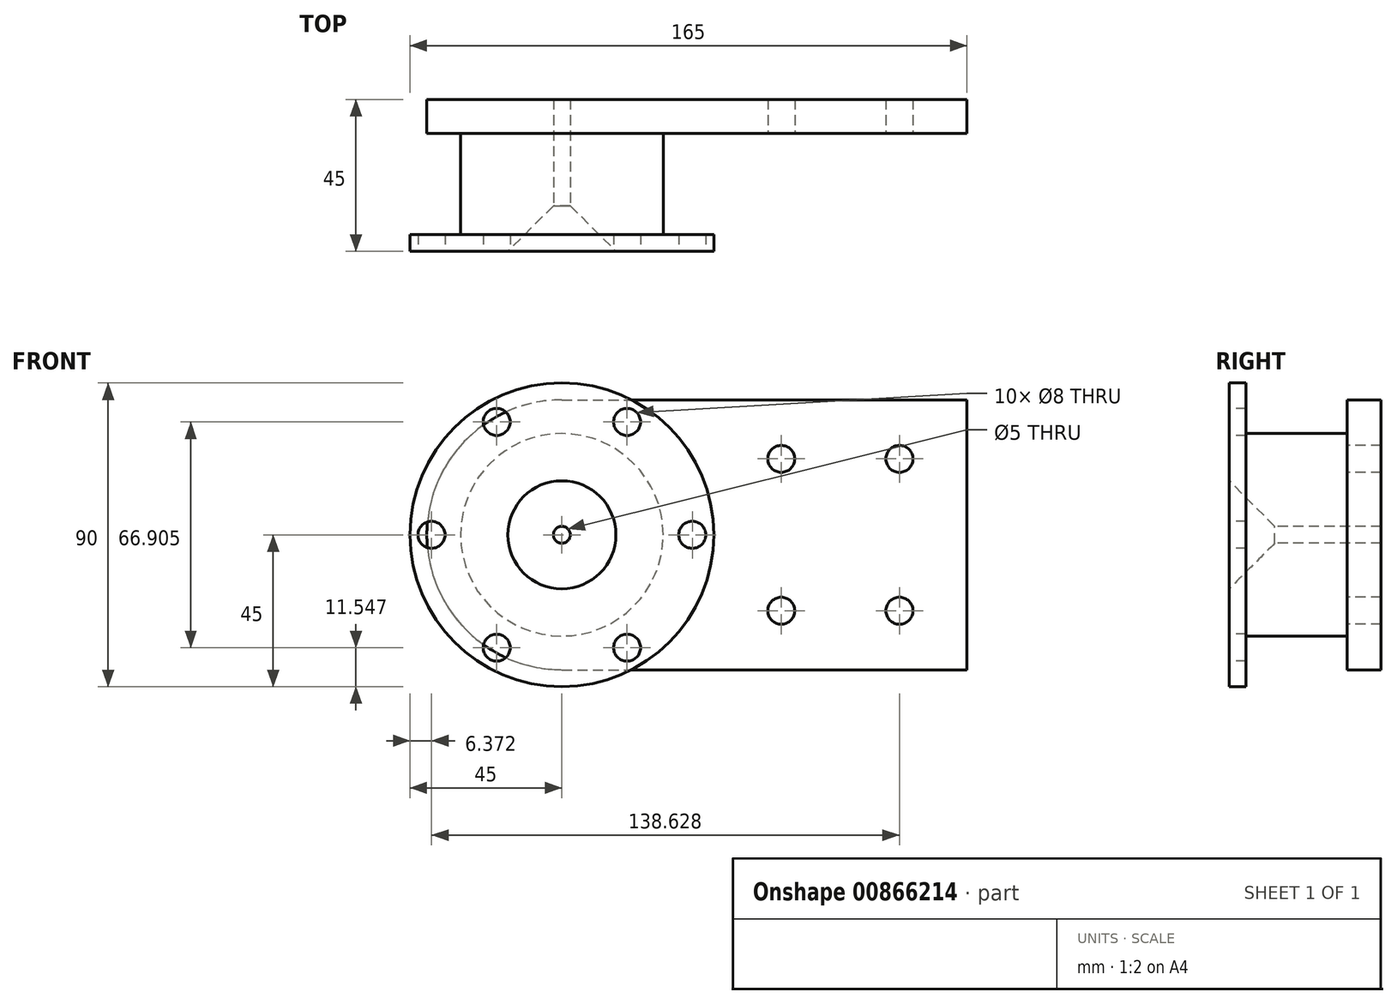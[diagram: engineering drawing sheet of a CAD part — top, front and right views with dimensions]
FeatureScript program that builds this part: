
annotation { "Feature Type Name" : "Feature", "Feature Type Description" : "" }
export const myFeature = defineFeature(function(context is Context, id is Id, definition is map)
    precondition{}
    {
        {
            var Q0;
            Q0=qCreatedBy(makeId("Front.planeOp"),FACE);
            var sketch = newSketch(context, id + "F0", { "sketchPlane" : qUnion([Q0])});
            skArc(sketch, "E0", {"start": v(0, 40) * mm, "mid": v(-40, 0) * mm, "end": v(0, -40) * mm});
            skLineSegment(sketch, "E1", {"start": v(0, 40) * mm, "end": v(120, 40) * mm});
            skLineSegment(sketch, "E2", {"start": v(120, 40) * mm, "end": v(120, -40) * mm});
            skLineSegment(sketch, "E3", {"start": v(0, -40) * mm, "end": v(120, -40) * mm});
            skSolve(sketch);
        }
        {
            var Q0;
            Q0=makeQuery(id+"F0.imprint","IMPRINT",FACE,{"disambiguationData":[TD([[makeQuery(id+"F0.imprint","IMPRINT",EDGE,{"derivedFrom":sQuery(id+"F0.wireOp",EDGE,"E0")}),1.0]])]});
            extrude(context, id + "F1", {"entities" : qUnion([Q0]), "depth" : 10 * mm, "offsetDistance" : 25 * mm});
        }
        {
            var Q0;
            Q0=makeQuery(id+"F1.opExtrude","CAP_FACE",FACE,{"disambiguationData":[OSD([sQuery(id+"F0.wireOp",EDGE,"E0"),sQuery(id+"F0.wireOp",EDGE,"E1"),sQuery(id+"F0.wireOp",EDGE,"E2"),sQuery(id+"F0.wireOp",EDGE,"E3")])],"isStart":false});
            var sketch = newSketch(context, id + "F2", { "sketchPlane" : qUnion([Q0])});
            skCircle(sketch, "E4", {"center": v(0, 0) * mm, "radius": 30 * mm});
            skSolve(sketch);
        }
        {
            var Q0;
            Q0 = qSketchRegion(id + "F2", true);
            extrude(context, id + "F3", {"entities" : qUnion([Q0]), "operationType" : NewBodyOperationType.ADD, "depth" : 30 * mm, "offsetDistance" : 25 * mm});
        }
        {
            var Q0;
            Q0=makeQuery(id+"F3.opExtrude","CAP_FACE",FACE,{"disambiguationData":[OSD([sQuery(id+"F2.wireOp",EDGE,"E4")])],"isStart":false});
            var sketch = newSketch(context, id + "F4", { "sketchPlane" : qUnion([Q0])});
            skCircle(sketch, "E5.0", {"center": v(0, 0) * mm, "radius": 45 * mm});
            skSolve(sketch);
        }
        {
            var Q0;
            Q0=makeQuery(id+"F4.imprint","IMPRINT",FACE,{"disambiguationData":[TD([[makeQuery(id+"F4.imprint","IMPRINT",EDGE,{"derivedFrom":makeQuery(id+"F3.opExtrude","CAP_EDGE",EDGE,{"disambiguationData":[OSD([sQuery(id+"F2.wireOp",EDGE,"E4")])],"isStart":false})}),1.0]])]});
            var Q1;
            Q1=makeQuery(id+"F4.imprint","IMPRINT",FACE,{"disambiguationData":[TD([[makeQuery(id+"F4.imprint","IMPRINT",EDGE,{"derivedFrom":sQuery(id+"F4.wireOp",EDGE,"E5.0")}),1.0]])]});
            extrude(context, id + "F5", {"entities" : qUnion([Q0, Q1]), "operationType" : NewBodyOperationType.ADD, "depth" : 5 * mm, "offsetDistance" : 25 * mm});
        }
        {
            var Q0;
            Q0=makeQuery(id+"F5.opExtrude","CAP_FACE",FACE,{"disambiguationData":[OSD([sQuery(id+"F4.wireOp",EDGE,"E5.0")])],"isStart":false});
            var sketch = newSketch(context, id + "F6", { "sketchPlane" : qUnion([Q0])});
            skLineSegment(sketch, "E6", {"start": v(0, 0) * mm, "end": v(45, 0) * mm, "construction": true});
            skCircle(sketch, "E7", {"center": v(38.63, 0) * mm, "radius": 4 * mm});
            skCircle(sketch, "E8.1.0", {"center": v(19.31, 33.45) * mm, "radius": 4 * mm});
            skCircle(sketch, "E8.2.0", {"center": v(-19.31, 33.45) * mm, "radius": 4 * mm});
            skCircle(sketch, "E8.3.0", {"center": v(-38.63, 0) * mm, "radius": 4 * mm});
            skCircle(sketch, "E8.4.0", {"center": v(-19.31, -33.45) * mm, "radius": 4 * mm});
            skCircle(sketch, "E8.5.0", {"center": v(19.31, -33.45) * mm, "radius": 4 * mm});
            skPoint(sketch, "E8.center", {"position": v(0, 0) * mm});
            skSolve(sketch);
        }
        {
            var Q0;
            Q0=makeQuery(id+"F6.imprint","IMPRINT",FACE,{"disambiguationData":[TD([[makeQuery(id+"F6.imprint","IMPRINT",EDGE,{"derivedFrom":sQuery(id+"F6.wireOp",EDGE,"E8.2.0")}),1.0]])]});
            var Q1;
            Q1=makeQuery(id+"F6.imprint","IMPRINT",FACE,{"disambiguationData":[TD([[makeQuery(id+"F6.imprint","IMPRINT",EDGE,{"derivedFrom":sQuery(id+"F6.wireOp",EDGE,"E8.1.0")}),1.0]])]});
            var Q2;
            Q2=makeQuery(id+"F6.imprint","IMPRINT",FACE,{"disambiguationData":[TD([[makeQuery(id+"F6.imprint","IMPRINT",EDGE,{"derivedFrom":sQuery(id+"F6.wireOp",EDGE,"E7")}),1.0]])]});
            var Q3;
            Q3=makeQuery(id+"F6.imprint","IMPRINT",FACE,{"disambiguationData":[TD([[makeQuery(id+"F6.imprint","IMPRINT",EDGE,{"derivedFrom":sQuery(id+"F6.wireOp",EDGE,"E8.5.0")}),1.0]])]});
            var Q4;
            Q4=makeQuery(id+"F6.imprint","IMPRINT",FACE,{"disambiguationData":[TD([[makeQuery(id+"F6.imprint","IMPRINT",EDGE,{"derivedFrom":sQuery(id+"F6.wireOp",EDGE,"E8.4.0")}),1.0]])]});
            var Q5;
            Q5=makeQuery(id+"F6.imprint","IMPRINT",FACE,{"disambiguationData":[TD([[makeQuery(id+"F6.imprint","IMPRINT",EDGE,{"derivedFrom":sQuery(id+"F6.wireOp",EDGE,"E8.3.0")}),1.0]])]});
            var Q6;
            Q6=makeQuery(id+"F5.opExtrude","CAP_FACE",FACE,{"disambiguationData":[OSD([sQuery(id+"F4.wireOp",EDGE,"E5.0")])],"isStart":true});
            extrude(context, id + "F7", {"entities" : qUnion([Q0, Q1, Q2, Q3, Q4, Q5]), "operationType" : NewBodyOperationType.REMOVE, "endBound" : BoundingType.UP_TO_SURFACE, "oppositeDirection" : true, "depth" : 25 * mm, "endBoundEntityFace" : qUnion([Q6]), "offsetDistance" : 25 * mm});
        }
        {
            var Q0;
            Q0=makeQuery(id+"F1.opExtrude","CAP_FACE",FACE,{"disambiguationData":[OSD([sQuery(id+"F0.wireOp",EDGE,"E0"),sQuery(id+"F0.wireOp",EDGE,"E1"),sQuery(id+"F0.wireOp",EDGE,"E2"),sQuery(id+"F0.wireOp",EDGE,"E3")])],"isStart":false});
            var sketch = newSketch(context, id + "F8", { "sketchPlane" : qUnion([Q0])});
            skLineSegment(sketch, "E9", {"start": v(120, 0) * mm, "end": v(45.7, 0) * mm, "construction": true});
            skLineSegment(sketch, "E10", {"start": v(120, 22.5) * mm, "end": v(49.41, 22.5) * mm, "construction": true});
            skCircle(sketch, "E11", {"center": v(65, 22.5) * mm, "radius": 4 * mm});
            skCircle(sketch, "E12", {"center": v(100, 22.5) * mm, "radius": 4 * mm});
            skCircle(sketch, "E13.MirrorC", {"center": v(65, -22.5) * mm, "radius": 4 * mm});
            skCircle(sketch, "E14.MirrorC", {"center": v(100, -22.5) * mm, "radius": 4 * mm});
            skSolve(sketch);
        }
        {
            var Q0;
            Q0 = qSketchRegion(id + "F8", true);
            extrude(context, id + "F9", {"entities" : qUnion([Q0]), "operationType" : NewBodyOperationType.REMOVE, "endBound" : BoundingType.THROUGH_ALL, "oppositeDirection" : true, "depth" : 25 * mm, "offsetDistance" : 25 * mm});
        }
        {
            var Q0;
            Q0=makeQuery(id+"F5.opExtrude","CAP_FACE",FACE,{"disambiguationData":[OSD([sQuery(id+"F4.wireOp",EDGE,"E5.0")])],"isStart":false});
            var sketch = newSketch(context, id + "F10", { "sketchPlane" : qUnion([Q0])});
            skPoint(sketch, "E15", {"position": v(0, 0) * mm});
            skSolve(sketch);
        }
        {
            var Q0;
            Q0=sQuery(id+"F10.wireOp",VERTEX,"E15");
            var Q1;
            Q1=makeQuery(id+"F1.opExtrude","SWEPT_BODY",BODY,{"disambiguationData":[OSD([sQuery(id+"F0.wireOp",EDGE,"E0"),sQuery(id+"F0.wireOp",EDGE,"E1"),sQuery(id+"F0.wireOp",EDGE,"E2"),sQuery(id+"F0.wireOp",EDGE,"E3")])]});
            hole(context, id + "F11", {"style" : HoleStyle.C_SINK, "endStyle" : HoleEndStyle.THROUGH, "holeDiameter" : 5 * mm, "cSinkDiameter" : 32 * mm, "cSinkAngle" : 90 * degree, "majorDiameter" : 5 * mm, "isTappedThrough" : true, "tappedDepth" : 12 * mm, "tapClearance" : 3, "locations" : qUnion([Q0]), "scope" : qUnion([Q1])});
        }
    });
